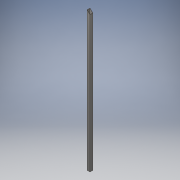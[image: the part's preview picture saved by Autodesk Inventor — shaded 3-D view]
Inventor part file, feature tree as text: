
AUTODESK INVENTOR PART (.ipt)
format: ipt  version: 2019 (Build 230136000, 136)  size: 153,088 bytes
history: native  units: mm
features: extrude x3, sketch x3, projected_geometry x1
ambient origin geometry x8: Origin, YZ Plane, XZ Plane, XY Plane, X Axis, Y Axis, Z Axis, Center Point
bodies: Solid1 (feature_tree)
feature tree (7):
  extrude  "Extrusion1"  Depth=30.0mm
  sketch  "Sketch2"  dims[d2=2.5mm d3=2.5mm]
  extrude  "Extrusion2"  Depth=2.5mm
  extrude  "Extrusion3"  TaperAngle=45.0deg  [1 undecoded]
  sketch  "Sketch3"  dims[d4=1400.0mm d5=0.0mm d6=45.0deg d7=45.0deg d8=0.0mm d9=0.0mm d10=0.0mm d11=0.0mm d12=0.0mm d13=0.0mm d20=450.0mm d21=1000.0mm d22=1220.0mm]
  sketch  "Sketch1"  dims[d0=30.0mm d1=30.0mm]
  projected_geometry  "Projected Loop1"
note: 1 required parameter value undecoded (feature->parameter linkage not recoverable at this tier; creation-order binding heuristic only, values carry confidence <= 0.55)
